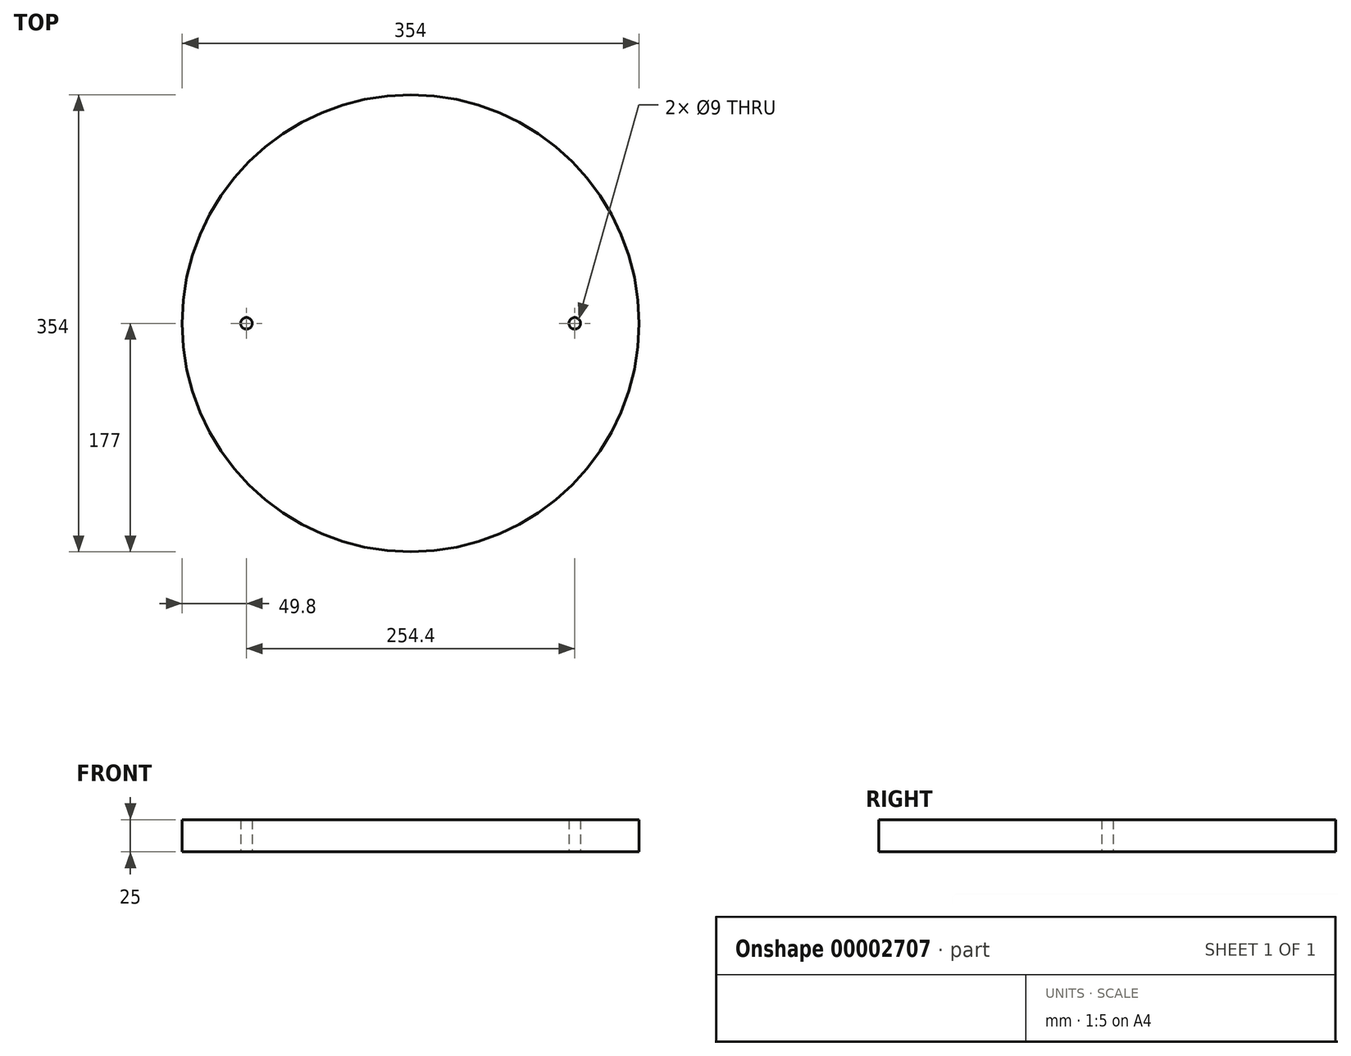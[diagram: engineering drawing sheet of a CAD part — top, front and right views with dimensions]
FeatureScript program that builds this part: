
annotation { "Feature Type Name" : "Feature", "Feature Type Description" : "" }
export const myFeature = defineFeature(function(context is Context, id is Id, definition is map)
    precondition{}
    {
        {
            var Q0;
            Q0=qCreatedBy(makeId("Top.planeOp"),FACE);
            var sketch = newSketch(context, id + "F0", { "sketchPlane" : qUnion([Q0])});
            skCircle(sketch, "E0", {"center": v(0, 0) * mm, "radius": 177 * mm});
            skLineSegment(sketch, "E1", {"start": v(-194.35, 0) * mm, "end": v(210.83, 0) * mm, "construction": true});
            skCircle(sketch, "E2", {"center": v(-127.2, 0) * mm, "radius": 4.5 * mm});
            skLineSegment(sketch, "E3", {"start": v(0, 49.62) * mm, "end": v(0, -58.59) * mm, "construction": true});
            skCircle(sketch, "E4.0.MirrorC", {"center": v(127.2, 0) * mm, "radius": 4.5 * mm});
            skSolve(sketch);
        }
        {
            var Q0;
            Q0=makeQuery(id+"F0.imprint","IMPRINT",FACE,{"disambiguationData":[TD([[makeQuery(id+"F0.imprint","IMPRINT",EDGE,{"derivedFrom":sQuery(id+"F0.wireOp",EDGE,"E0")}),1.0]])]});
            extrude(context, id + "F1", {"entities" : qUnion([Q0]), "depth" : 25 * mm});
        }
    });
